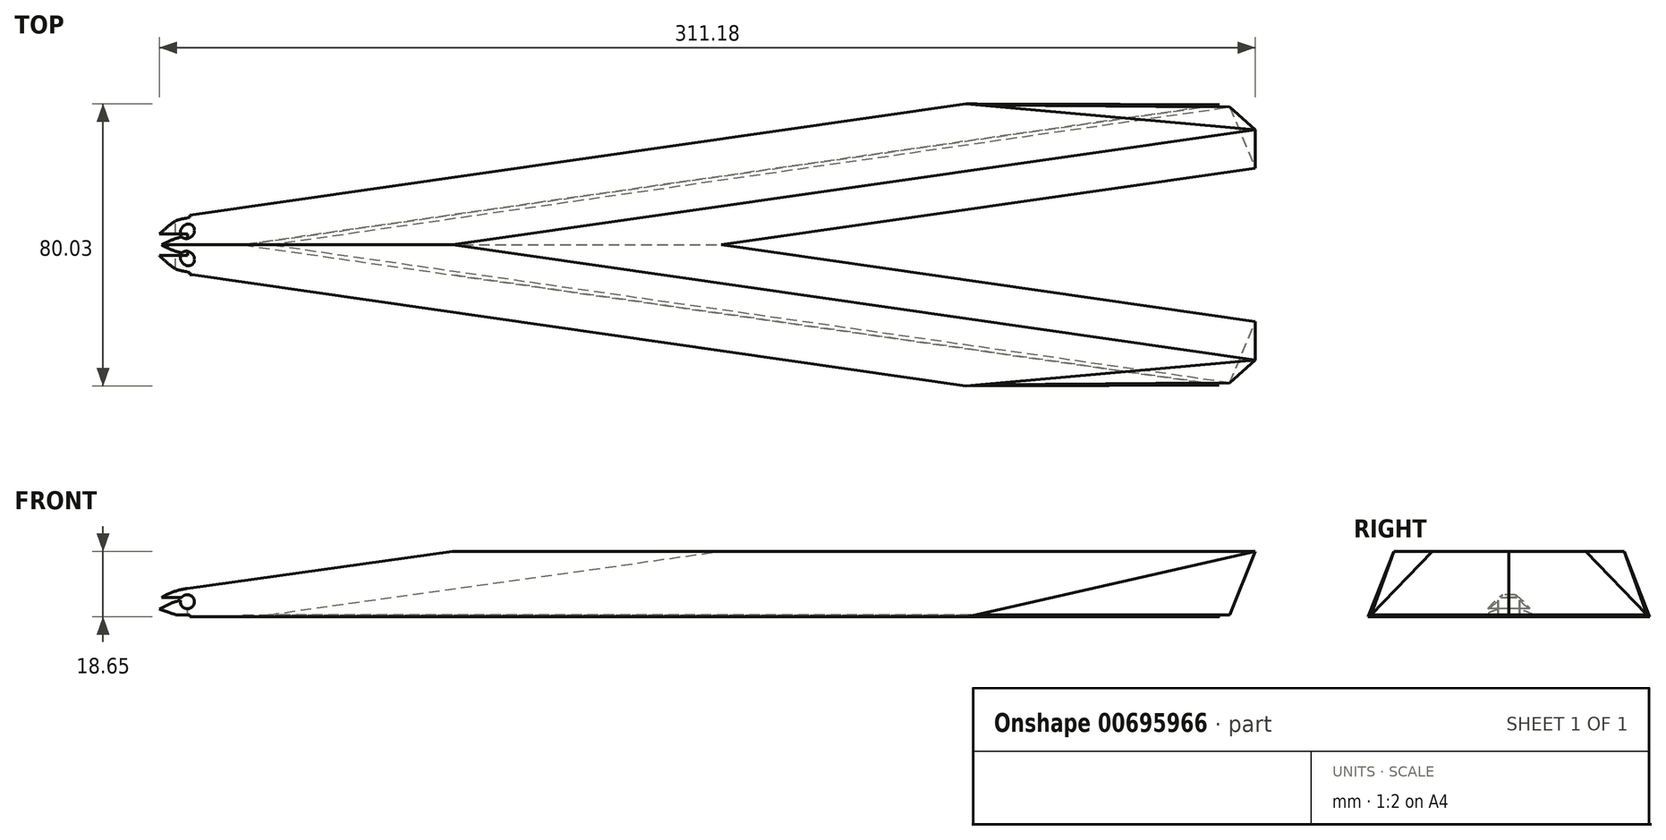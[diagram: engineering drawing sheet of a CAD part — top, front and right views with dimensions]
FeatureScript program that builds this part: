
annotation { "Feature Type Name" : "Feature", "Feature Type Description" : "" }
export const myFeature = defineFeature(function(context is Context, id is Id, definition is map)
    precondition{}
    {
        {
            var Q0;
            Q0=qCreatedBy(makeId("Top.planeOp"),FACE);
            var sketch = newSketch(context, id + "F0", { "sketchPlane" : qUnion([Q0])});
            skPoint(sketch, "E0.middle", {"position": v(0, 0) * mm});
            skLineSegment(sketch, "E1", {"start": v(-412.82, -3.14) * mm, "end": v(-111.11, 40.17) * mm});
            skLineSegment(sketch, "E2", {"start": v(-111.11, 40.17) * mm, "end": v(-34.8, 40.17) * mm});
            skLineSegment(sketch, "E3", {"start": v(-314.62, 0) * mm, "end": v(-34.8, 40.17) * mm});
            skLineSegment(sketch, "E4", {"start": v(-314.62, 0) * mm, "end": v(0, 0) * mm, "construction": true});
            skLineSegment(sketch, "E5.MirrorCS", {"start": v(-314.62, 0) * mm, "end": v(-34.8, -40.17) * mm});
            skLineSegment(sketch, "E6.MirrorCS", {"start": v(-412.82, 3.14) * mm, "end": v(-111.11, -40.17) * mm});
            skLineSegment(sketch, "E7.MirrorCS", {"start": v(-111.11, -40.17) * mm, "end": v(-34.8, -40.17) * mm});
            skLineSegment(sketch, "E8", {"start": v(-111.11, 40.17) * mm, "end": v(-340.87, 7.19) * mm, "construction": true});
            skLineSegment(sketch, "E9", {"start": v(-340.87, 7.19) * mm, "end": v(-340.87, -7.19) * mm, "construction": true});
            skLineSegment(sketch, "E10", {"start": v(-340.87, 0) * mm, "end": v(0, 0) * mm, "construction": true});
            skSolve(sketch);
        }
        {
            var Q0;
            Q0=qCreatedBy(makeId("Top.planeOp"),FACE);
            cPlane(context, id + "F1", {"entities" : qUnion([Q0]), "cplaneType" : CPlaneType.OFFSET, "offset" : 19.05 * mm, "width" : 152.4 * mm, "height" : 152.4 * mm});
        }
        {
            var Q0;
            Q0=qCreatedBy(id+"F1.planeOp",FACE);
            var sketch = newSketch(context, id + "F2", { "sketchPlane" : qUnion([Q0])});
            skLineSegment(sketch, "E11", {"start": v(0, 0) * mm, "end": v(-27.18, 0) * mm, "construction": true});
            skLineSegment(sketch, "E12", {"start": v(-27.18, 32.73) * mm, "end": v(-27.23, 21.78) * mm});
            skLineSegment(sketch, "E13", {"start": v(-255.16, 0) * mm, "end": v(-27.18, 32.73) * mm});
            skLineSegment(sketch, "E14", {"start": v(-27.18, 32.73) * mm, "end": v(-27.18, -32.73) * mm, "construction": true});
            skLineSegment(sketch, "E15", {"start": v(-178.9, 0) * mm, "end": v(-27.23, 21.78) * mm});
            skLineSegment(sketch, "E16.MirrorCS", {"start": v(-178.9, 0) * mm, "end": v(-27.23, -21.78) * mm});
            skLineSegment(sketch, "E17.MirrorCS", {"start": v(-255.16, 0) * mm, "end": v(-27.18, -32.73) * mm});
            skLineSegment(sketch, "E18.MirrorCS", {"start": v(-27.18, -32.73) * mm, "end": v(-27.23, -21.78) * mm});
            skSolve(sketch);
        }
        {
            var Q0;
            {var subQ0=sQuery(id+"F0.wireOp",EDGE,"E2");Q0=makeQuery(id+"F0.imprint","IMPRINT",FACE,{"disambiguationData":[TD([[makeQuery(id+"F0.imprint","IMPRINT",EDGE,{"derivedFrom":subQ0}),-1.0]])]});}
            var Q1;
            Q1=makeQuery(id+"F2.imprint","IMPRINT",FACE,{"disambiguationData":[TD([[makeQuery(id+"F2.imprint","IMPRINT",EDGE,{"derivedFrom":sQuery(id+"F2.wireOp",EDGE,"E12")}),-1.0]])]});
            loft(context, id + "F3", {"sheetProfilesArray" : [{ "sheetProfileEntities" : qUnion([Q0]) }, { "sheetProfileEntities" : qUnion([Q1]) }]});
        }
        {
            var Q0;
            Q0=qCreatedBy(makeId("Right.planeOp"),FACE);
            cPlane(context, id + "F4", {"entities" : qUnion([Q0]), "cplaneType" : CPlaneType.OFFSET, "offset" : 340.87 * mm, "oppositeDirection" : true, "width" : 152.4 * mm, "height" : 152.4 * mm});
        }
        {
            var Q0;
            Q0=qCreatedBy(id+"F4.planeOp",FACE);
            var sketch = newSketch(context, id + "F5", { "sketchPlane" : qUnion([Q0])});
            skLineSegment(sketch, "E19.bottom", {"start": v(-16.87, -11.02) * mm, "end": v(16.87, -11.02) * mm});
            skLineSegment(sketch, "E19.top", {"start": v(-16.87, 11.02) * mm, "end": v(16.87, 11.02) * mm});
            skLineSegment(sketch, "E19.left", {"start": v(-16.87, -11.02) * mm, "end": v(-16.87, 11.02) * mm});
            skLineSegment(sketch, "E19.right", {"start": v(16.87, -11.02) * mm, "end": v(16.87, 11.02) * mm});
            skPoint(sketch, "E19.middle", {"position": v(0, 0) * mm});
            skSolve(sketch);
        }
        {
            var Q0;
            Q0=makeQuery(id+"F5.imprint","IMPRINT",FACE,{"disambiguationData":[TD([[makeQuery(id+"F5.imprint","IMPRINT",EDGE,{"derivedFrom":sQuery(id+"F5.wireOp",EDGE,"E19.bottom")}),1.0]])]});
            extrude(context, id + "F6", {"entities" : qUnion([Q0]), "operationType" : NewBodyOperationType.REMOVE, "oppositeDirection" : true, "depth" : 79.5 * mm, "offsetDistance" : 25.4 * mm});
        }
        {
            var Q0;
            Q0=makeQuery(id+"F6.boolean.opBoolean","INTERSECT",EDGE,{"derivedFrom":[makeQuery(id+"F3.opLoft","SWEPT_FACE",FACE,{"disambiguationData":[OSD([sQuery(id+"F0.wireOp",EDGE,"E1"),sQuery(id+"F0.wireOp",EDGE,"E6.MirrorCS"),sQuery(id+"F0.wireOp",EDGE,"E7.MirrorCS"),sQuery(id+"F2.wireOp",EDGE,"E13"),sQuery(id+"F2.wireOp",EDGE,"E17.MirrorCS"),sQuery(id+"F2.wireOp",EDGE,"E18.MirrorCS")])]}),makeQuery(id+"F6.opExtrude","CAP_FACE",FACE,{"disambiguationData":[OSD([sQuery(id+"F5.wireOp",EDGE,"E19.bottom"),sQuery(id+"F5.wireOp",EDGE,"E19.top"),sQuery(id+"F5.wireOp",EDGE,"E19.left"),sQuery(id+"F5.wireOp",EDGE,"E19.right")])],"isStart":true})]});
            var Q1;
            Q1=makeQuery(id+"F6.boolean.opBoolean","INTERSECT",EDGE,{"derivedFrom":[makeQuery(id+"F3.opLoft","SWEPT_FACE",FACE,{"disambiguationData":[OSD([sQuery(id+"F0.wireOp",EDGE,"E1"),sQuery(id+"F0.wireOp",EDGE,"E2"),sQuery(id+"F0.wireOp",EDGE,"E6.MirrorCS"),sQuery(id+"F2.wireOp",EDGE,"E12"),sQuery(id+"F2.wireOp",EDGE,"E13"),sQuery(id+"F2.wireOp",EDGE,"E17.MirrorCS")])]}),makeQuery(id+"F6.opExtrude","CAP_FACE",FACE,{"disambiguationData":[OSD([sQuery(id+"F5.wireOp",EDGE,"E19.bottom"),sQuery(id+"F5.wireOp",EDGE,"E19.top"),sQuery(id+"F5.wireOp",EDGE,"E19.left"),sQuery(id+"F5.wireOp",EDGE,"E19.right")])],"isStart":true})]});
            var Q2;
            {var subQ0=sQuery(id+"F0.wireOp",EDGE,"E2");Q2=makeQuery(id+"F6.boolean.opBoolean","INTERSECT",EDGE,{"derivedFrom":[makeQuery(id+"F3.opLoft","CAP_FACE",FACE,{"disambiguationData":[OSD([makeQuery(id+"F0.imprint","IMPRINT",FACE,{"disambiguationData":[TD([[makeQuery(id+"F0.imprint","IMPRINT",EDGE,{"derivedFrom":subQ0}),-1.0]])]})])],"isStart":true}),makeQuery(id+"F6.opExtrude","CAP_FACE",FACE,{"disambiguationData":[OSD([sQuery(id+"F5.wireOp",EDGE,"E19.bottom"),sQuery(id+"F5.wireOp",EDGE,"E19.top"),sQuery(id+"F5.wireOp",EDGE,"E19.left"),sQuery(id+"F5.wireOp",EDGE,"E19.right")])],"isStart":true})]});}
            chamfer(context, id + "F7", {"entities" : qUnion([Q0, Q1, Q2]), "width" : 2.54 * mm, "tangentPropagation" : true});
        }
        {
            var Q0;
            {var subQ0=sQuery(id+"F0.wireOp",EDGE,"E2");var subQ5=makeQuery(id+"F3.opLoft","CAP_FACE",FACE,{"disambiguationData":[OSD([makeQuery(id+"F0.imprint","IMPRINT",FACE,{"disambiguationData":[TD([[makeQuery(id+"F0.imprint","IMPRINT",EDGE,{"derivedFrom":subQ0}),-1.0]])]})])],"isStart":true});Q0=makeQuery(id+"F7.opChamfer","BLEND_EDGE",EDGE,{"blendedFrom":[makeQuery(id+"F6.boolean.opBoolean","INTERSECT",EDGE,{"derivedFrom":[subQ5,makeQuery(id+"F6.opExtrude","CAP_FACE",FACE,{"disambiguationData":[OSD([sQuery(id+"F5.wireOp",EDGE,"E19.bottom"),sQuery(id+"F5.wireOp",EDGE,"E19.top"),sQuery(id+"F5.wireOp",EDGE,"E19.left"),sQuery(id+"F5.wireOp",EDGE,"E19.right")])],"isStart":true})]}),subQ5],"blendedInto":[subQ5]});}
            var Q1;
            {var subQ0=makeQuery(id+"F3.opLoft","SWEPT_FACE",FACE,{"disambiguationData":[OSD([sQuery(id+"F0.wireOp",EDGE,"E1"),sQuery(id+"F0.wireOp",EDGE,"E6.MirrorCS"),sQuery(id+"F0.wireOp",EDGE,"E7.MirrorCS"),sQuery(id+"F2.wireOp",EDGE,"E13"),sQuery(id+"F2.wireOp",EDGE,"E17.MirrorCS"),sQuery(id+"F2.wireOp",EDGE,"E18.MirrorCS")])]});Q1=makeQuery(id+"F7.opChamfer","BLEND_EDGE",EDGE,{"blendedFrom":[makeQuery(id+"F6.boolean.opBoolean","INTERSECT",EDGE,{"derivedFrom":[subQ0,makeQuery(id+"F6.opExtrude","CAP_FACE",FACE,{"disambiguationData":[OSD([sQuery(id+"F5.wireOp",EDGE,"E19.bottom"),sQuery(id+"F5.wireOp",EDGE,"E19.top"),sQuery(id+"F5.wireOp",EDGE,"E19.left"),sQuery(id+"F5.wireOp",EDGE,"E19.right")])],"isStart":true})]}),subQ0],"blendedInto":[subQ0]});}
            var Q2;
            {var subQ0=makeQuery(id+"F3.opLoft","SWEPT_FACE",FACE,{"disambiguationData":[OSD([sQuery(id+"F0.wireOp",EDGE,"E1"),sQuery(id+"F0.wireOp",EDGE,"E2"),sQuery(id+"F0.wireOp",EDGE,"E6.MirrorCS"),sQuery(id+"F2.wireOp",EDGE,"E12"),sQuery(id+"F2.wireOp",EDGE,"E13"),sQuery(id+"F2.wireOp",EDGE,"E17.MirrorCS")])]});Q2=makeQuery(id+"F7.opChamfer","BLEND_EDGE",EDGE,{"blendedFrom":[makeQuery(id+"F6.boolean.opBoolean","INTERSECT",EDGE,{"derivedFrom":[subQ0,makeQuery(id+"F6.opExtrude","CAP_FACE",FACE,{"disambiguationData":[OSD([sQuery(id+"F5.wireOp",EDGE,"E19.bottom"),sQuery(id+"F5.wireOp",EDGE,"E19.top"),sQuery(id+"F5.wireOp",EDGE,"E19.left"),sQuery(id+"F5.wireOp",EDGE,"E19.right")])],"isStart":true})]}),subQ0],"blendedInto":[subQ0]});}
            fillet(context, id + "F8", {"entities" : qUnion([Q0, Q1, Q2]), "radius" : 25.9 * mm, "tangentPropagation" : true, "allowEdgeOverflow" : false});
        }
        {
            var Q0;
            {var subQ0=sQuery(id+"F0.wireOp",EDGE,"E2");Q0=makeQuery(id+"F0.imprint","IMPRINT",FACE,{"disambiguationData":[TD([[makeQuery(id+"F0.imprint","IMPRINT",EDGE,{"derivedFrom":subQ0}),-1.0]])]});}
            var sketch = newSketch(context, id + "F9", { "sketchPlane" : qUnion([Q0])});
            skPoint(sketch, "E20.0", {"position": v(-340.87, 0) * mm});
            skLineSegment(sketch, "E21", {"start": v(-340.87, 0) * mm, "end": v(-334.77, 0) * mm, "construction": true});
            skSolve(sketch);
        }
        {
            var Q0;
            Q0=sQuery(id+"F0.wireOp",EDGE,"E9");
            cPoint(context, id + "F10", {"entities" : qUnion([Q0]), "parameter" : 0.5});
        }
        {
            var Q0;
            Q0=sQuery(id+"F2.wireOp",VERTEX,"E16.MirrorCS.start");
            var Q1;
            Q1=sQuery(id+"F2.wireOp",VERTEX,"E13.start");
            var Q2;
            Q2 = qCreatedBy(id + "F10" ,VERTEX);
            cPlane(context, id + "F11", {"entities" : qUnion([Q0, Q1, Q2]), "cplaneType" : CPlaneType.THREE_POINT, "offset" : 25.4 * mm, "width" : 152.4 * mm, "height" : 152.4 * mm});
        }
        {
            var Q0;
            Q0=qCreatedBy(id+"F11.planeOp",FACE);
            var sketch = newSketch(context, id + "F12", { "sketchPlane" : qUnion([Q0])});
            skPoint(sketch, "E22.0", {"position": v(340.87, 0) * mm});
            skLineSegment(sketch, "E23", {"start": v(340.87, 0) * mm, "end": v(330.41, 0) * mm, "construction": true});
            skLineSegment(sketch, "E24", {"start": v(330.41, 0) * mm, "end": v(330.41, 4.72) * mm, "construction": true});
            skCircle(sketch, "E25", {"center": v(330.41, 4.72) * mm, "radius": 2.02 * mm});
            skSolve(sketch);
        }
        {
            var Q0;
            Q0 = qSketchRegion(id + "F12", true);
            extrude(context, id + "F13", {"entities" : qUnion([Q0]), "operationType" : NewBodyOperationType.REMOVE, "depth" : 25.4 * mm, "offsetDistance" : 25.4 * mm, "hasSecondDirection" : true, "secondDirectionOppositeDirection" : true, "secondDirectionDepth" : 25.4 * mm});
        }
        {
            var Q0;
            Q0=qCreatedBy(id+"F4.planeOp",FACE);
            var sketch = newSketch(context, id + "F14", { "sketchPlane" : qUnion([Q0])});
            skLineSegment(sketch, "E26.bottom", {"start": v(-3.05, -5.97) * mm, "end": v(3.05, -5.97) * mm});
            skLineSegment(sketch, "E26.top", {"start": v(-3.05, 5.97) * mm, "end": v(3.05, 5.97) * mm});
            skLineSegment(sketch, "E26.left", {"start": v(-3.05, -5.97) * mm, "end": v(-3.05, 5.97) * mm});
            skLineSegment(sketch, "E26.right", {"start": v(3.05, -5.97) * mm, "end": v(3.05, 5.97) * mm});
            skPoint(sketch, "E26.middle", {"position": v(0, 0) * mm});
            skSolve(sketch);
        }
        {
            var Q0;
            Q0=makeQuery(id+"F14.imprint","IMPRINT",FACE,{"disambiguationData":[TD([[makeQuery(id+"F14.imprint","IMPRINT",EDGE,{"derivedFrom":sQuery(id+"F14.wireOp",EDGE,"E26.bottom")}),1.0]])]});
            extrude(context, id + "F15", {"entities" : qUnion([Q0]), "operationType" : NewBodyOperationType.REMOVE, "depth" : 10.44 * mm, "offsetDistance" : 25.4 * mm});
        }
        {
            var Q0;
            {var subQ0=sQuery(id+"F0.wireOp",EDGE,"E2");Q0=makeQuery(id+"F3.opLoft","CAP_FACE",FACE,{"disambiguationData":[OSD([makeQuery(id+"F0.imprint","IMPRINT",FACE,{"disambiguationData":[TD([[makeQuery(id+"F0.imprint","IMPRINT",EDGE,{"derivedFrom":subQ0}),-1.0]])]})])],"isStart":true});}
            var sketch = newSketch(context, id + "F16", { "sketchPlane" : qUnion([Q0])});
            skLineSegment(sketch, "E27.bottom", {"start": v(-383.46, 55.4) * mm, "end": v(-23.02, 55.4) * mm});
            skLineSegment(sketch, "E27.top", {"start": v(-383.46, -59.8) * mm, "end": v(-23.02, -59.8) * mm});
            skLineSegment(sketch, "E27.left", {"start": v(-383.46, 55.4) * mm, "end": v(-383.46, -59.8) * mm});
            skLineSegment(sketch, "E27.right", {"start": v(-23.02, 55.4) * mm, "end": v(-23.02, -59.8) * mm});
            skSolve(sketch);
        }
        {
            var Q0;
            Q0=makeQuery(id+"F16.imprint","IMPRINT",FACE,{"disambiguationData":[TD([[makeQuery(id+"F16.imprint","IMPRINT",EDGE,{"derivedFrom":sQuery(id+"F16.wireOp",EDGE,"E27.bottom")}),-1.0]])]});
            extrude(context, id + "F17", {"entities" : qUnion([Q0]), "operationType" : NewBodyOperationType.REMOVE, "oppositeDirection" : true, "depth" : 1.02 * mm, "offsetDistance" : 25.4 * mm});
        }
        {
            var Q0;
            {var subQ0=sQuery(id+"F0.wireOp",EDGE,"E2");Q0=makeQuery(id+"F17.boolean.opBoolean","COPY",FACE,{"derivedFrom":makeQuery(id+"F17.opExtrude","SWEPT_FACE",FACE,{"disambiguationData":[OSD([makeQuery(id+"F0.imprint","IMPRINT",FACE,{"disambiguationData":[TD([[makeQuery(id+"F0.imprint","IMPRINT",EDGE,{"derivedFrom":subQ0}),-1.0]])]}),sQuery(id+"F5.wireOp",EDGE,"E19.bottom"),sQuery(id+"F5.wireOp",EDGE,"E19.top"),sQuery(id+"F5.wireOp",EDGE,"E19.left"),sQuery(id+"F5.wireOp",EDGE,"E19.right")])]})});}
            var sketch = newSketch(context, id + "F18", { "sketchPlane" : qUnion([Q0])});
            skLineSegment(sketch, "E28", {"start": v(8.87, 0) * mm, "end": v(-8.87, 0) * mm});
            skLineSegment(sketch, "E29", {"start": v(-7.83, 0.4) * mm, "end": v(8.47, 0.4) * mm});
            skLineSegment(sketch, "E30", {"start": v(-7.83, 0.4) * mm, "end": v(-15.03, 0.4) * mm});
            skLineSegment(sketch, "E31", {"start": v(-15.03, 0.4) * mm, "end": v(-68.45, 0.4) * mm});
            skLineSegment(sketch, "E32", {"start": v(-8.87, 0) * mm, "end": v(-68.83, 0) * mm});
            skLineSegment(sketch, "E33", {"start": v(-68.83, 0) * mm, "end": v(-68.45, 0.4) * mm});
            skLineSegment(sketch, "E34", {"start": v(8.87, 0) * mm, "end": v(44.06, 0) * mm});
            skLineSegment(sketch, "E35", {"start": v(44.06, 0) * mm, "end": v(46.48, 0.4) * mm});
            skLineSegment(sketch, "E36", {"start": v(46.48, 0.4) * mm, "end": v(8.47, 0.4) * mm});
            skSolve(sketch);
        }
        {
            var Q0;
            Q0 = qSketchRegion(id + "F18", true);
            extrude(context, id + "F19", {"entities" : qUnion([Q0]), "operationType" : NewBodyOperationType.REMOVE, "oppositeDirection" : true, "depth" : 304.8 * mm, "offsetDistance" : 25.4 * mm});
        }
        {
            var Q0;
            {var subQ0=sQuery(id+"F5.wireOp",EDGE,"E19.right");var subQ1=sQuery(id+"F5.wireOp",EDGE,"E19.left");var subQ2=sQuery(id+"F5.wireOp",EDGE,"E19.top");var subQ3=sQuery(id+"F5.wireOp",EDGE,"E19.bottom");var subQ4=sQuery(id+"F0.wireOp",EDGE,"E7.MirrorCS");var subQ5=sQuery(id+"F0.wireOp",EDGE,"E6.MirrorCS");var subQ6=sQuery(id+"F0.wireOp",EDGE,"E1");var subQ7=sQuery(id+"F0.wireOp",EDGE,"E2");Q0=makeQuery(id+"F15.boolean.opBoolean","INTERSECT",VERTEX,{"derivedFrom":[makeQuery(id+"F8.opFillet","BLEND_FACE",FACE,{"disambiguationData":[OSD([makeQuery(id+"F0.imprint","IMPRINT",FACE,{"disambiguationData":[TD([[makeQuery(id+"F0.imprint","IMPRINT",EDGE,{"derivedFrom":subQ7}),-1.0]])]}),subQ3,subQ2,subQ1,subQ0])]}),makeQuery(id+"F8.opFillet","BLEND_FACE",FACE,{"disambiguationData":[OSD([subQ6,subQ5,subQ4,sQuery(id+"F2.wireOp",EDGE,"E13"),sQuery(id+"F2.wireOp",EDGE,"E17.MirrorCS"),sQuery(id+"F2.wireOp",EDGE,"E18.MirrorCS"),subQ3,subQ2,subQ1,subQ0])]}),makeQuery(id+"F15.opExtrude","SWEPT_FACE",FACE,{"disambiguationData":[OSD([sQuery(id+"F14.wireOp",EDGE,"E26.left")])]})]});}
            var Q1;
            {var subQ0=sQuery(id+"F5.wireOp",EDGE,"E19.right");var subQ1=sQuery(id+"F5.wireOp",EDGE,"E19.left");var subQ2=sQuery(id+"F5.wireOp",EDGE,"E19.top");var subQ3=sQuery(id+"F5.wireOp",EDGE,"E19.bottom");var subQ4=sQuery(id+"F0.wireOp",EDGE,"E5.MirrorCS");var subQ5=sQuery(id+"F0.wireOp",EDGE,"E3");var subQ6=sQuery(id+"F0.wireOp",EDGE,"E2");var subQ7=sQuery(id+"F0.wireOp",EDGE,"E1");var subQ8=sQuery(id+"F0.wireOp",EDGE,"E6.MirrorCS");var subQ10=sQuery(id+"F0.wireOp",EDGE,"E7.MirrorCS");var subQ11=makeQuery(id+"F0.imprint","IMPRINT",FACE,{"disambiguationData":[TD([[makeQuery(id+"F0.imprint","IMPRINT",EDGE,{"derivedFrom":subQ6}),-1.0]])]});var subQ12=sQuery(id+"F2.wireOp",EDGE,"E18.MirrorCS");var subQ13=sQuery(id+"F2.wireOp",EDGE,"E17.MirrorCS");var subQ14=sQuery(id+"F2.wireOp",EDGE,"E13");var subQ15=makeQuery(id+"F8.opFillet","BLEND_FACE",FACE,{"disambiguationData":[OSD([subQ11,subQ3,subQ2,subQ1,subQ0])]});Q1=makeQuery(id+"F17.boolean.opBoolean","INTERSECT",VERTEX,{"derivedFrom":[subQ15,makeQuery(id+"F15.boolean.opBoolean","SPLIT",FACE,{"disambiguationData":[TD([makeQuery(id+"F15.opExtrude","SWEPT_FACE",FACE,{"disambiguationData":[OSD([sQuery(id+"F14.wireOp",EDGE,"E26.left")])]})])],"derivedFrom":makeQuery(id+"F8.opFillet","BLEND_FACE",FACE,{"disambiguationData":[OSD([subQ7,subQ8,subQ10,subQ14,subQ13,subQ12,subQ3,subQ2,subQ1,subQ0])]})}),makeQuery(id+"F17.opExtrude","CAP_FACE",FACE,{"disambiguationData":[OSD([subQ7,subQ6,subQ5,subQ4,subQ8,subQ10,subQ11,subQ3,subQ2,subQ1,subQ0,sQuery(id+"F16.wireOp",EDGE,"E27.bottom"),sQuery(id+"F16.wireOp",EDGE,"E27.top"),sQuery(id+"F16.wireOp",EDGE,"E27.left"),sQuery(id+"F16.wireOp",EDGE,"E27.right")])],"isStart":false})]});}
            var Q2;
            {var subQ0=sQuery(id+"F5.wireOp",EDGE,"E19.right");var subQ1=sQuery(id+"F5.wireOp",EDGE,"E19.left");var subQ2=sQuery(id+"F5.wireOp",EDGE,"E19.top");var subQ3=sQuery(id+"F5.wireOp",EDGE,"E19.bottom");var subQ4=sQuery(id+"F0.wireOp",EDGE,"E5.MirrorCS");var subQ5=sQuery(id+"F0.wireOp",EDGE,"E3");var subQ6=sQuery(id+"F0.wireOp",EDGE,"E2");var subQ7=sQuery(id+"F0.wireOp",EDGE,"E1");var subQ8=sQuery(id+"F0.wireOp",EDGE,"E6.MirrorCS");var subQ10=sQuery(id+"F0.wireOp",EDGE,"E7.MirrorCS");var subQ11=makeQuery(id+"F0.imprint","IMPRINT",FACE,{"disambiguationData":[TD([[makeQuery(id+"F0.imprint","IMPRINT",EDGE,{"derivedFrom":subQ6}),-1.0]])]});Q2=makeQuery(id+"F17.boolean.opBoolean","INTERSECT",VERTEX,{"derivedFrom":[makeQuery(id+"F15.boolean.opBoolean","COPY",FACE,{"derivedFrom":makeQuery(id+"F15.opExtrude","SWEPT_FACE",FACE,{"disambiguationData":[OSD([sQuery(id+"F14.wireOp",EDGE,"E26.left")])]})}),makeQuery(id+"F8.opFillet","BLEND_FACE",FACE,{"disambiguationData":[OSD([subQ11,subQ3,subQ2,subQ1,subQ0])]}),makeQuery(id+"F17.opExtrude","CAP_FACE",FACE,{"disambiguationData":[OSD([subQ7,subQ6,subQ5,subQ4,subQ8,subQ10,subQ11,subQ3,subQ2,subQ1,subQ0,sQuery(id+"F16.wireOp",EDGE,"E27.bottom"),sQuery(id+"F16.wireOp",EDGE,"E27.top"),sQuery(id+"F16.wireOp",EDGE,"E27.left"),sQuery(id+"F16.wireOp",EDGE,"E27.right")])],"isStart":false})]});}
            cPlane(context, id + "F20", {"entities" : qUnion([Q0, Q1, Q2]), "cplaneType" : CPlaneType.THREE_POINT, "offset" : 25.4 * mm, "width" : 152.4 * mm, "height" : 152.4 * mm});
        }
        {
            var Q0;
            Q0=qCreatedBy(id+"F20.planeOp",FACE);
            var sketch = newSketch(context, id + "F21", { "sketchPlane" : qUnion([Q0])});
            skLineSegment(sketch, "E37.bottom", {"start": v(-321.4, 7.73) * mm, "end": v(-314.29, 7.73) * mm});
            skLineSegment(sketch, "E37.top", {"start": v(-321.4, -9.26) * mm, "end": v(-314.29, -9.26) * mm});
            skLineSegment(sketch, "E37.left", {"start": v(-321.4, 7.73) * mm, "end": v(-321.4, -9.26) * mm});
            skLineSegment(sketch, "E37.right", {"start": v(-314.29, 7.73) * mm, "end": v(-314.29, -9.26) * mm});
            skSolve(sketch);
        }
        {
            var Q0;
            Q0 = qSketchRegion(id + "F21", true);
            extrude(context, id + "F22", {"entities" : qUnion([Q0]), "operationType" : NewBodyOperationType.REMOVE, "oppositeDirection" : true, "depth" : 1.02 * mm, "offsetDistance" : 25.4 * mm, "hasSecondDirection" : true, "secondDirectionOppositeDirection" : false, "secondDirectionDepth" : 25.4 * mm});
        }
        {
            var Q0;
            Q0=makeQuery(id+"F3.opLoft","MID_CAP_VERTEX",VERTEX,{"disambiguationData":[OSD([sQuery(id+"F2.wireOp",EDGE,"E17.MirrorCS"),sQuery(id+"F2.wireOp",EDGE,"E18.MirrorCS")])],"capPos":1.0});
            var Q1;
            {var subQ0=sQuery(id+"F0.wireOp",EDGE,"E5.MirrorCS");var subQ1=sQuery(id+"F0.wireOp",EDGE,"E3");var subQ2=sQuery(id+"F0.wireOp",EDGE,"E2");var subQ3=sQuery(id+"F0.wireOp",EDGE,"E1");var subQ4=sQuery(id+"F0.wireOp",EDGE,"E6.MirrorCS");var subQ6=sQuery(id+"F0.wireOp",EDGE,"E7.MirrorCS");var subQ7=sQuery(id+"F2.wireOp",EDGE,"E18.MirrorCS");var subQ8=sQuery(id+"F2.wireOp",EDGE,"E16.MirrorCS");Q1=makeQuery(id+"F17.boolean.opBoolean","INTERSECT",VERTEX,{"derivedFrom":[makeQuery(id+"F3.opLoft","SWEPT_FACE",FACE,{"disambiguationData":[OSD([subQ1,subQ0,subQ6,sQuery(id+"F2.wireOp",EDGE,"E15"),subQ8,subQ7])]}),makeQuery(id+"F3.opLoft","SWEPT_FACE",FACE,{"disambiguationData":[OSD([subQ0,subQ4,subQ6,subQ8,sQuery(id+"F2.wireOp",EDGE,"E17.MirrorCS"),subQ7])]}),makeQuery(id+"F17.opExtrude","CAP_FACE",FACE,{"disambiguationData":[OSD([subQ3,subQ2,subQ1,subQ0,subQ4,subQ6,makeQuery(id+"F0.imprint","IMPRINT",FACE,{"disambiguationData":[TD([[makeQuery(id+"F0.imprint","IMPRINT",EDGE,{"derivedFrom":subQ2}),-1.0]])]}),sQuery(id+"F5.wireOp",EDGE,"E19.bottom"),sQuery(id+"F5.wireOp",EDGE,"E19.top"),sQuery(id+"F5.wireOp",EDGE,"E19.left"),sQuery(id+"F5.wireOp",EDGE,"E19.right"),sQuery(id+"F16.wireOp",EDGE,"E27.bottom"),sQuery(id+"F16.wireOp",EDGE,"E27.top"),sQuery(id+"F16.wireOp",EDGE,"E27.left"),sQuery(id+"F16.wireOp",EDGE,"E27.right")])],"isStart":false})]});}
            var Q2;
            {var subQ0=sQuery(id+"F2.wireOp",EDGE,"E18.MirrorCS");var subQ1=sQuery(id+"F2.wireOp",EDGE,"E17.MirrorCS");var subQ2=sQuery(id+"F0.wireOp",EDGE,"E7.MirrorCS");var subQ3=sQuery(id+"F0.wireOp",EDGE,"E6.MirrorCS");Q2=makeQuery(id+"F19.boolean.opBoolean","INTERSECT",VERTEX,{"derivedFrom":[makeQuery(id+"F3.opLoft","SWEPT_FACE",FACE,{"disambiguationData":[OSD([sQuery(id+"F0.wireOp",EDGE,"E5.MirrorCS"),subQ3,subQ2,sQuery(id+"F2.wireOp",EDGE,"E16.MirrorCS"),subQ1,subQ0])]}),makeQuery(id+"F3.opLoft","SWEPT_FACE",FACE,{"disambiguationData":[OSD([sQuery(id+"F0.wireOp",EDGE,"E1"),subQ3,subQ2,sQuery(id+"F2.wireOp",EDGE,"E13"),subQ1,subQ0])]}),makeQuery(id+"F19.opExtrude","SWEPT_FACE",FACE,{"disambiguationData":[OSD([sQuery(id+"F18.wireOp",EDGE,"E36")])]})]});}
            cPlane(context, id + "F23", {"entities" : qUnion([Q0, Q1, Q2]), "cplaneType" : CPlaneType.THREE_POINT, "offset" : 25.4 * mm, "width" : 152.4 * mm, "height" : 152.4 * mm});
        }
        {
            var Q0;
            Q0=qCreatedBy(id+"F23.planeOp",FACE);
            var sketch = newSketch(context, id + "F24", { "sketchPlane" : qUnion([Q0])});
            skPoint(sketch, "E38.0", {"position": v(-109.62, -13) * mm});
            skPoint(sketch, "E39.0", {"position": v(-27.46, 7) * mm});
            skPoint(sketch, "E40.0", {"position": v(-34.67, -12.15) * mm});
            skLineSegment(sketch, "E41", {"start": v(-109.62, -13) * mm, "end": v(-27.46, 7) * mm});
            skLineSegment(sketch, "E42", {"start": v(-34.67, -12.15) * mm, "end": v(-27.46, 7) * mm});
            skLineSegment(sketch, "E43", {"start": v(-34.67, -12.15) * mm, "end": v(-109.62, -13) * mm});
            skSolve(sketch);
        }
        {
            var Q1;
            Q1=makeQuery(id+"F3.opLoft","MID_CAP_VERTEX",VERTEX,{"disambiguationData":[OSD([sQuery(id+"F2.wireOp",EDGE,"E16.MirrorCS"),sQuery(id+"F2.wireOp",EDGE,"E18.MirrorCS")])],"capPos":1.0});
            var Q2;
            Q2=makeQuery(id+"F24.imprint","IMPRINT",FACE,{"disambiguationData":[TD([[makeQuery(id+"F24.imprint","IMPRINT",EDGE,{"derivedFrom":sQuery(id+"F24.wireOp",EDGE,"E41")}),-1.0]])]});
            loft(context, id + "F25", {"operationType" : NewBodyOperationType.ADD, "sheetProfilesArray" : [{ "sheetProfileEntities" : qUnion([Q1]) }, { "sheetProfileEntities" : qUnion([Q2]) }]});
        }
        {
            var Q0;
            Q0=makeQuery(id+"F3.opLoft","MID_CAP_VERTEX",VERTEX,{"disambiguationData":[OSD([sQuery(id+"F2.wireOp",EDGE,"E12"),sQuery(id+"F2.wireOp",EDGE,"E13")])],"capPos":1.0});
            var Q1;
            {var subQ0=sQuery(id+"F0.wireOp",EDGE,"E5.MirrorCS");var subQ1=sQuery(id+"F0.wireOp",EDGE,"E3");var subQ2=sQuery(id+"F0.wireOp",EDGE,"E2");var subQ3=sQuery(id+"F0.wireOp",EDGE,"E1");var subQ4=sQuery(id+"F0.wireOp",EDGE,"E6.MirrorCS");var subQ6=sQuery(id+"F0.wireOp",EDGE,"E7.MirrorCS");var subQ7=sQuery(id+"F2.wireOp",EDGE,"E15");var subQ8=sQuery(id+"F2.wireOp",EDGE,"E12");Q1=makeQuery(id+"F17.boolean.opBoolean","INTERSECT",VERTEX,{"derivedFrom":[makeQuery(id+"F3.opLoft","SWEPT_FACE",FACE,{"disambiguationData":[OSD([subQ3,subQ2,subQ1,subQ8,sQuery(id+"F2.wireOp",EDGE,"E13"),subQ7])]}),makeQuery(id+"F3.opLoft","SWEPT_FACE",FACE,{"disambiguationData":[OSD([subQ2,subQ1,subQ0,subQ8,subQ7,sQuery(id+"F2.wireOp",EDGE,"E16.MirrorCS")])]}),makeQuery(id+"F17.opExtrude","CAP_FACE",FACE,{"disambiguationData":[OSD([subQ3,subQ2,subQ1,subQ0,subQ4,subQ6,makeQuery(id+"F0.imprint","IMPRINT",FACE,{"disambiguationData":[TD([[makeQuery(id+"F0.imprint","IMPRINT",EDGE,{"derivedFrom":subQ2}),-1.0]])]}),sQuery(id+"F5.wireOp",EDGE,"E19.bottom"),sQuery(id+"F5.wireOp",EDGE,"E19.top"),sQuery(id+"F5.wireOp",EDGE,"E19.left"),sQuery(id+"F5.wireOp",EDGE,"E19.right"),sQuery(id+"F16.wireOp",EDGE,"E27.bottom"),sQuery(id+"F16.wireOp",EDGE,"E27.top"),sQuery(id+"F16.wireOp",EDGE,"E27.left"),sQuery(id+"F16.wireOp",EDGE,"E27.right")])],"isStart":false})]});}
            var Q2;
            {var subQ0=sQuery(id+"F2.wireOp",EDGE,"E13");var subQ1=sQuery(id+"F2.wireOp",EDGE,"E12");var subQ2=sQuery(id+"F0.wireOp",EDGE,"E2");var subQ3=sQuery(id+"F0.wireOp",EDGE,"E1");Q2=makeQuery(id+"F19.boolean.opBoolean","INTERSECT",VERTEX,{"derivedFrom":[makeQuery(id+"F3.opLoft","SWEPT_FACE",FACE,{"disambiguationData":[OSD([subQ3,subQ2,sQuery(id+"F0.wireOp",EDGE,"E3"),subQ1,subQ0,sQuery(id+"F2.wireOp",EDGE,"E15")])]}),makeQuery(id+"F3.opLoft","SWEPT_FACE",FACE,{"disambiguationData":[OSD([subQ3,subQ2,sQuery(id+"F0.wireOp",EDGE,"E6.MirrorCS"),subQ1,subQ0,sQuery(id+"F2.wireOp",EDGE,"E17.MirrorCS")])]}),makeQuery(id+"F19.opExtrude","SWEPT_FACE",FACE,{"disambiguationData":[OSD([sQuery(id+"F18.wireOp",EDGE,"E29"),sQuery(id+"F18.wireOp",EDGE,"E30"),sQuery(id+"F18.wireOp",EDGE,"E31")])]})]});}
            cPlane(context, id + "F26", {"entities" : qUnion([Q0, Q1, Q2]), "cplaneType" : CPlaneType.THREE_POINT, "offset" : 25.4 * mm, "width" : 152.4 * mm, "height" : 152.4 * mm});
        }
        {
            var Q0;
            Q0=qCreatedBy(id+"F26.planeOp",FACE);
            var sketch = newSketch(context, id + "F27", { "sketchPlane" : qUnion([Q0])});
            skPoint(sketch, "E44.0", {"position": v(-27.46, 7) * mm});
            skPoint(sketch, "E45.0", {"position": v(-34.67, -12.15) * mm});
            skPoint(sketch, "E46.0", {"position": v(-109.65, -13) * mm});
            skLineSegment(sketch, "E47", {"start": v(-27.46, 7) * mm, "end": v(-34.67, -12.15) * mm});
            skLineSegment(sketch, "E48", {"start": v(-109.65, -13) * mm, "end": v(-27.46, 7) * mm});
            skLineSegment(sketch, "E49", {"start": v(-34.67, -12.15) * mm, "end": v(-109.65, -13) * mm});
            skSolve(sketch);
        }
        {
            var Q1;
            Q1=makeQuery(id+"F3.opLoft","MID_CAP_VERTEX",VERTEX,{"disambiguationData":[OSD([sQuery(id+"F2.wireOp",EDGE,"E12"),sQuery(id+"F2.wireOp",EDGE,"E15")])],"capPos":1.0});
            var Q2;
            Q2=makeQuery(id+"F27.imprint","IMPRINT",FACE,{"disambiguationData":[TD([[makeQuery(id+"F27.imprint","IMPRINT",EDGE,{"derivedFrom":sQuery(id+"F27.wireOp",EDGE,"E47")}),-1.0]])]});
            loft(context, id + "F28", {"operationType" : NewBodyOperationType.ADD, "sheetProfilesArray" : [{ "sheetProfileEntities" : qUnion([Q1]) }, { "sheetProfileEntities" : qUnion([Q2]) }]});
        }
    });
